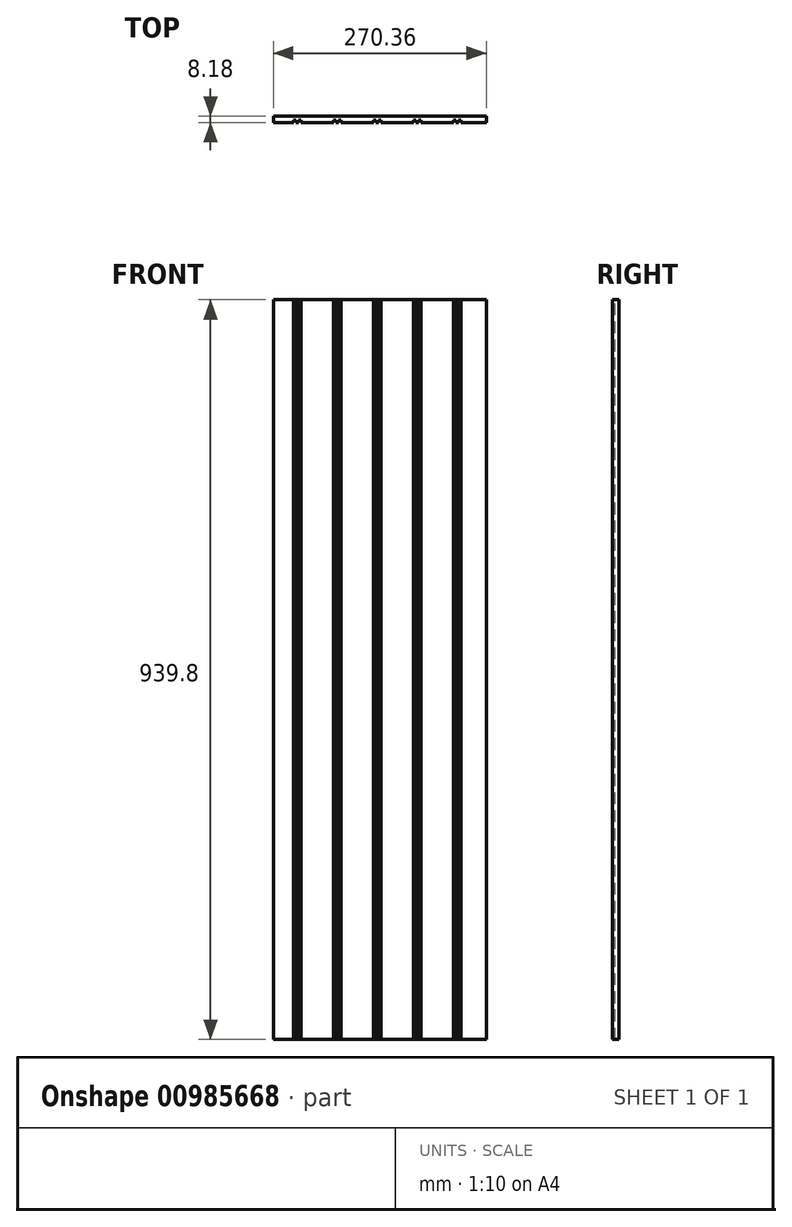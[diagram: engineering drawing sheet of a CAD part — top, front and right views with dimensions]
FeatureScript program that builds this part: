
annotation { "Feature Type Name" : "Feature", "Feature Type Description" : "" }
export const myFeature = defineFeature(function(context is Context, id is Id, definition is map)
    precondition{}
    {
        {
            var Q0;
            Q0=qCreatedBy(makeId("Front.planeOp"),FACE);
            var sketch = newSketch(context, id + "F0", { "sketchPlane" : qUnion([Q0])});
            skLineSegment(sketch, "E0.bottom", {"start": v(135.18, 469.9) * mm, "end": v(-135.18, 469.9) * mm});
            skLineSegment(sketch, "E0.top", {"start": v(135.18, -469.9) * mm, "end": v(-135.18, -469.9) * mm});
            skLineSegment(sketch, "E0.left", {"start": v(135.18, 469.9) * mm, "end": v(135.18, -469.9) * mm});
            skLineSegment(sketch, "E0.right", {"start": v(-135.18, 469.9) * mm, "end": v(-135.18, -469.9) * mm});
            skPoint(sketch, "E0.middle", {"position": v(0, 0) * mm});
            skSolve(sketch);
        }
        {
            var Q0;
            Q0=qSketchRegion(id+"F0",true);
            extrude(context, id + "F1", {"entities" : qUnion([Q0]), "depth" : 8.18 * mm, "offsetDistance" : 25.4 * mm});
        }
        {
            var Q0;
            Q0=makeQuery(id+"F1.opExtrude","SWEPT_FACE",FACE,{"disambiguationData":[OSD([sQuery(id+"F0.wireOp",EDGE,"E0.bottom")])]});
            var sketch = newSketch(context, id + "F2", { "sketchPlane" : qUnion([Q0])});
            skLineSegment(sketch, "E1.bottom", {"start": v(-109.78, -8.18) * mm, "end": v(-106.6, -8.18) * mm});
            skLineSegment(sketch, "E1.top", {"start": v(-109.78, -5) * mm, "end": v(-106.6, -5) * mm});
            skLineSegment(sketch, "E1.left", {"start": v(-109.78, -8.18) * mm, "end": v(-109.78, -5) * mm});
            skLineSegment(sketch, "E1.right", {"start": v(-106.6, -8.18) * mm, "end": v(-106.6, -5) * mm});
            skLineSegment(sketch, "E2.bottom", {"start": v(-103.43, -5) * mm, "end": v(-100.25, -5) * mm});
            skLineSegment(sketch, "E2.top", {"start": v(-103.43, -8.18) * mm, "end": v(-100.25, -8.18) * mm});
            skLineSegment(sketch, "E2.left", {"start": v(-103.43, -5) * mm, "end": v(-103.43, -8.18) * mm});
            skLineSegment(sketch, "E2.right", {"start": v(-100.25, -5) * mm, "end": v(-100.25, -8.18) * mm});
            skLineSegment(sketch, "E3.1.0.0", {"start": v(-58.98, -5) * mm, "end": v(-55.8, -5) * mm});
            skLineSegment(sketch, "E3.1.0.1", {"start": v(-55.8, -8.18) * mm, "end": v(-55.8, -5) * mm});
            skLineSegment(sketch, "E3.1.0.2", {"start": v(-58.98, -8.18) * mm, "end": v(-58.98, -5) * mm});
            skLineSegment(sketch, "E3.1.0.3", {"start": v(-52.63, -5) * mm, "end": v(-49.45, -5) * mm});
            skLineSegment(sketch, "E3.1.0.4", {"start": v(-49.45, -5) * mm, "end": v(-49.45, -8.18) * mm});
            skLineSegment(sketch, "E3.1.0.5", {"start": v(-52.63, -5) * mm, "end": v(-52.63, -8.18) * mm});
            skLineSegment(sketch, "E3.1.0.6", {"start": v(-52.63, -8.18) * mm, "end": v(-49.45, -8.18) * mm});
            skLineSegment(sketch, "E3.1.0.7", {"start": v(-58.98, -8.18) * mm, "end": v(-55.8, -8.18) * mm});
            skLineSegment(sketch, "E3.2.0.0", {"start": v(-8.18, -5) * mm, "end": v(-5, -5) * mm});
            skLineSegment(sketch, "E3.2.0.1", {"start": v(-5, -8.18) * mm, "end": v(-5, -5) * mm});
            skLineSegment(sketch, "E3.2.0.2", {"start": v(-8.18, -8.18) * mm, "end": v(-8.18, -5) * mm});
            skLineSegment(sketch, "E3.2.0.3", {"start": v(-1.83, -5) * mm, "end": v(1.35, -5) * mm});
            skLineSegment(sketch, "E3.2.0.4", {"start": v(1.35, -5) * mm, "end": v(1.35, -8.18) * mm});
            skLineSegment(sketch, "E3.2.0.5", {"start": v(-1.83, -5) * mm, "end": v(-1.83, -8.18) * mm});
            skLineSegment(sketch, "E3.2.0.6", {"start": v(-1.83, -8.18) * mm, "end": v(1.35, -8.18) * mm});
            skLineSegment(sketch, "E3.2.0.7", {"start": v(-8.18, -8.18) * mm, "end": v(-5, -8.18) * mm});
            skLineSegment(sketch, "E3.direction1", {"start": v(-109.78, -5) * mm, "end": v(-58.98, -5) * mm, "construction": true});
            skLineSegment(sketch, "E4.0.3.0", {"start": v(42.62, -5) * mm, "end": v(45.8, -5) * mm});
            skLineSegment(sketch, "E4.3.3.0", {"start": v(45.8, -8.18) * mm, "end": v(45.8, -5) * mm});
            skLineSegment(sketch, "E4.6.3.0", {"start": v(42.62, -8.18) * mm, "end": v(42.62, -5) * mm});
            skLineSegment(sketch, "E4.9.3.0", {"start": v(48.97, -5) * mm, "end": v(52.15, -5) * mm});
            skLineSegment(sketch, "E4.12.3.0", {"start": v(52.15, -5) * mm, "end": v(52.15, -8.18) * mm});
            skLineSegment(sketch, "E4.15.3.0", {"start": v(48.97, -5) * mm, "end": v(48.97, -8.18) * mm});
            skLineSegment(sketch, "E4.18.3.0", {"start": v(48.97, -8.18) * mm, "end": v(52.15, -8.18) * mm});
            skLineSegment(sketch, "E4.21.3.0", {"start": v(42.62, -8.18) * mm, "end": v(45.8, -8.18) * mm});
            skLineSegment(sketch, "E5.0.4.0", {"start": v(93.42, -5) * mm, "end": v(96.6, -5) * mm});
            skLineSegment(sketch, "E5.3.4.0", {"start": v(96.6, -8.18) * mm, "end": v(96.6, -5) * mm});
            skLineSegment(sketch, "E5.6.4.0", {"start": v(93.42, -8.18) * mm, "end": v(93.42, -5) * mm});
            skLineSegment(sketch, "E5.9.4.0", {"start": v(99.77, -5) * mm, "end": v(102.95, -5) * mm});
            skLineSegment(sketch, "E5.12.4.0", {"start": v(102.95, -5) * mm, "end": v(102.95, -8.18) * mm});
            skLineSegment(sketch, "E5.15.4.0", {"start": v(99.77, -5) * mm, "end": v(99.77, -8.18) * mm});
            skLineSegment(sketch, "E5.18.4.0", {"start": v(99.77, -8.18) * mm, "end": v(102.95, -8.18) * mm});
            skLineSegment(sketch, "E5.21.4.0", {"start": v(93.42, -8.18) * mm, "end": v(96.6, -8.18) * mm});
            skSolve(sketch);
        }
        {
            var Q0;
            Q0=qSketchRegion(id+"F2",true);
            extrude(context, id + "F3", {"entities" : qUnion([Q0]), "operationType" : NewBodyOperationType.REMOVE, "endBound" : BoundingType.THROUGH_ALL, "oppositeDirection" : true, "depth" : 25.4 * mm, "offsetDistance" : 25.4 * mm});
        }
    });
